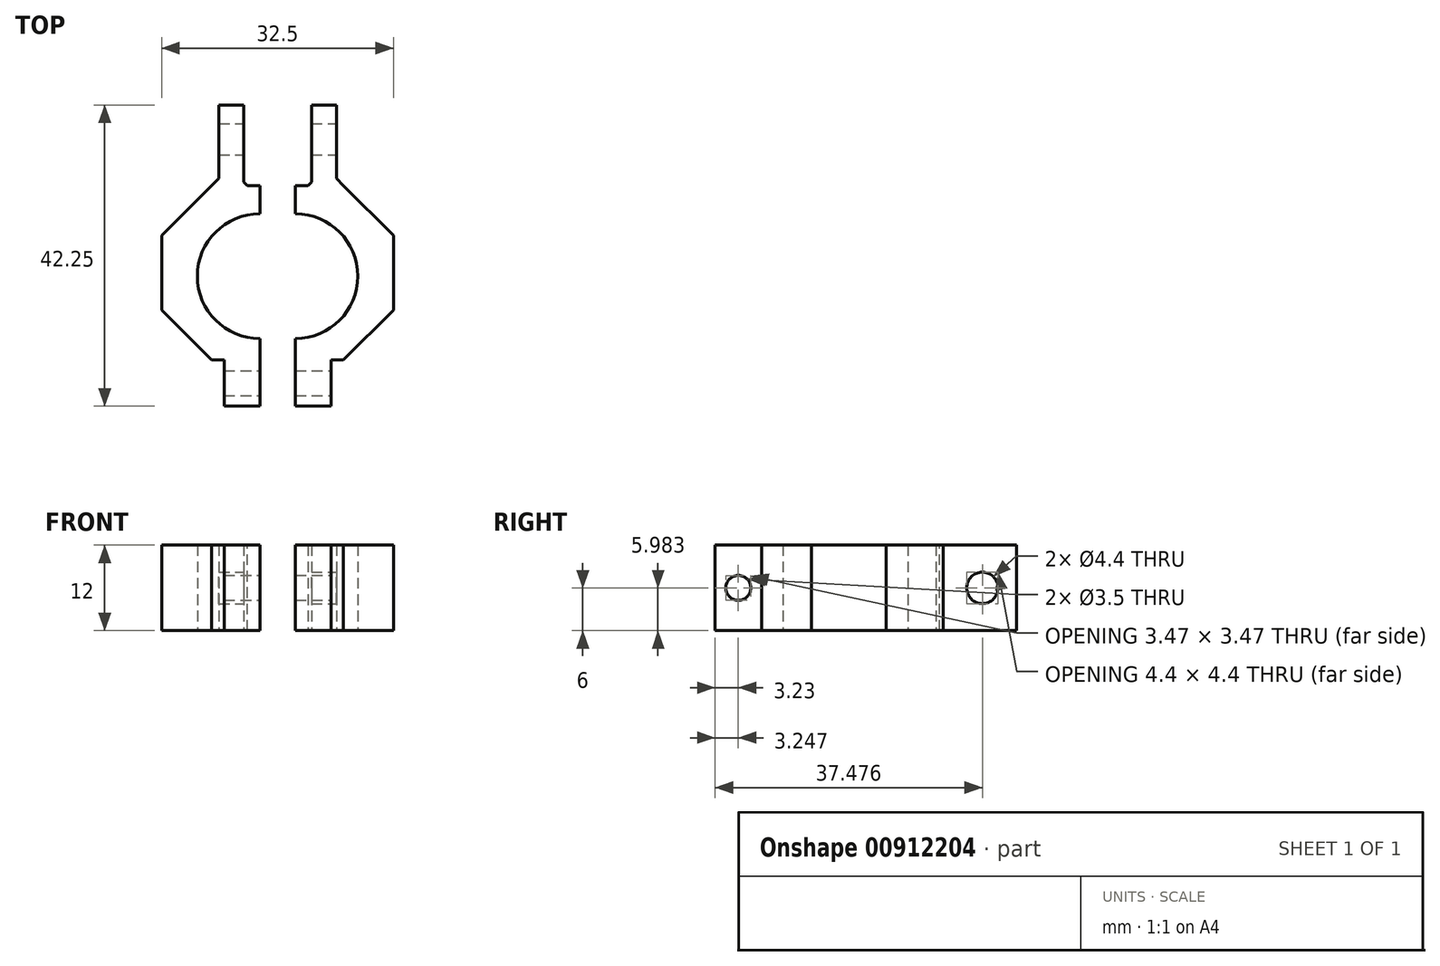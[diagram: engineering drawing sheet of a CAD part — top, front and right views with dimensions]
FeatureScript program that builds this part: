
annotation { "Feature Type Name" : "Feature", "Feature Type Description" : "" }
export const myFeature = defineFeature(function(context is Context, id is Id, definition is map)
    precondition{}
    {
        {
            var Q0;
            Q0=qCreatedBy(makeId("Top.planeOp"),FACE);
            var sketch = newSketch(context, id + "F0", { "sketchPlane" : qUnion([Q0])});
            skCircle(sketch, "E0", {"center": v(-3.1, 1.35) * mm, "radius": 8.75 * mm});
            skLineSegment(sketch, "E1", {"start": v(-11.85, 1.35) * mm, "end": v(-3.1, 1.35) * mm, "construction": true});
            skLineSegment(sketch, "E2", {"start": v(-3.1, 1.35) * mm, "end": v(5.65, 1.35) * mm, "construction": true});
            skLineSegment(sketch, "E3", {"start": v(-5.35, 1.35) * mm, "end": v(-5.35, 14.08) * mm, "construction": true});
            skLineSegment(sketch, "E4", {"start": v(-0.85, 14.08) * mm, "end": v(-0.85, 1.35) * mm, "construction": true});
            skLineSegment(sketch, "E5.bottom", {"start": v(-16.85, 25.35) * mm, "end": v(10.65, 25.35) * mm});
            skLineSegment(sketch, "E5.top", {"start": v(-16.85, -10.4) * mm, "end": v(10.65, -10.4) * mm});
            skLineSegment(sketch, "E5.left", {"start": v(-16.85, 25.35) * mm, "end": v(-16.85, -10.4) * mm});
            skLineSegment(sketch, "E5.right", {"start": v(10.65, 25.35) * mm, "end": v(10.65, -10.4) * mm});
            skLineSegment(sketch, "E6", {"start": v(-11.85, 1.35) * mm, "end": v(-16.85, 1.35) * mm, "construction": true});
            skLineSegment(sketch, "E7", {"start": v(5.65, 1.35) * mm, "end": v(10.65, 1.35) * mm, "construction": true});
            skLineSegment(sketch, "E8", {"start": v(-5.35, 14.08) * mm, "end": v(-5.35, 25.35) * mm});
            skLineSegment(sketch, "E9", {"start": v(-5.35, 14.08) * mm, "end": v(-0.85, 14.08) * mm});
            skLineSegment(sketch, "E10", {"start": v(-0.85, 14.08) * mm, "end": v(-0.85, 25.35) * mm});
            skLineSegment(sketch, "E11", {"start": v(-3.1, 1.35) * mm, "end": v(-3.1, -7.4) * mm});
            skLineSegment(sketch, "E12", {"start": v(-3.1, -7.4) * mm, "end": v(-3.1, -10.4) * mm});
            skLineSegment(sketch, "E13", {"start": v(-8.1, -10.4) * mm, "end": v(-8.1, -16.9) * mm});
            skLineSegment(sketch, "E14", {"start": v(-8.1, -16.9) * mm, "end": v(-3.1, -16.9) * mm});
            skLineSegment(sketch, "E15", {"start": v(-3.1, -16.9) * mm, "end": v(-3.1, -10.4) * mm});
            skLineSegment(sketch, "E16", {"start": v(-3.1, -16.9) * mm, "end": v(1.9, -16.9) * mm});
            skLineSegment(sketch, "E17", {"start": v(1.9, -16.9) * mm, "end": v(1.9, -10.4) * mm});
            skLineSegment(sketch, "E18", {"start": v(-3.1, 14.08) * mm, "end": v(-3.1, 10.1) * mm});
            skLineSegment(sketch, "E19", {"start": v(-8.85, 25.35) * mm, "end": v(-8.85, 14.08) * mm});
            skLineSegment(sketch, "E20", {"start": v(-8.85, 14.08) * mm, "end": v(-16.85, 14.08) * mm});
            skLineSegment(sketch, "E21", {"start": v(2.65, 25.35) * mm, "end": v(2.65, 14.08) * mm});
            skLineSegment(sketch, "E22", {"start": v(2.65, 14.08) * mm, "end": v(10.65, 14.08) * mm});
            skSolve(sketch);
        }
        {
            var Q0;
            {var subQ2=sQuery(id+"F0.wireOp",EDGE,"E13");Q0=makeQuery(id+"F0.imprint","IMPRINT",FACE,{"disambiguationData":[TD([[makeQuery(id+"F0.imprint","IMPRINT",EDGE,{"derivedFrom":subQ2}),1.0]])]});}
            var Q1;
            {var subQ1=sQuery(id+"F0.wireOp",EDGE,"E8");Q1=makeQuery(id+"F0.imprint","IMPRINT",FACE,{"disambiguationData":[TD([[makeQuery(id+"F0.imprint","IMPRINT",EDGE,{"derivedFrom":subQ1}),1.0]])]});}
            extrude(context, id + "F1", {"entities" : qUnion([Q0, Q1]), "depth" : 12 * mm, "offsetDistance" : 25 * mm});
        }
        {
            var Q0;
            {var subQ0=sQuery(id+"F0.wireOp",EDGE,"E15");Q0=makeQuery(id+"F0.imprint","IMPRINT",FACE,{"disambiguationData":[TD([[makeQuery(id+"F0.imprint","IMPRINT",EDGE,{"derivedFrom":subQ0}),-1.0]])]});}
            var Q1;
            {var subQ1=sQuery(id+"F0.wireOp",EDGE,"E10");Q1=makeQuery(id+"F0.imprint","IMPRINT",FACE,{"disambiguationData":[TD([[makeQuery(id+"F0.imprint","IMPRINT",EDGE,{"derivedFrom":subQ1}),-1.0]])]});}
            extrude(context, id + "F2", {"entities" : qUnion([Q0, Q1]), "depth" : 12 * mm, "offsetDistance" : 25 * mm});
        }
        {
            var Q0;
            Q0=makeQuery(id+"F1.opExtrude","SWEPT_EDGE",EDGE,{"disambiguationData":[OSD([sQuery(id+"F0.wireOp",EDGE,"E5.left"),sQuery(id+"F0.wireOp",EDGE,"E20")])]});
            var Q1;
            Q1=makeQuery(id+"F2.opExtrude","SWEPT_EDGE",EDGE,{"disambiguationData":[OSD([sQuery(id+"F0.wireOp",EDGE,"E5.right"),sQuery(id+"F0.wireOp",EDGE,"E22")])]});
            var Q2;
            Q2=makeQuery(id+"F1.opExtrude","SWEPT_EDGE",EDGE,{"disambiguationData":[OSD([sQuery(id+"F0.wireOp",EDGE,"E5.top"),sQuery(id+"F0.wireOp",EDGE,"E5.left")])]});
            var Q3;
            Q3=makeQuery(id+"F2.opExtrude","SWEPT_EDGE",EDGE,{"disambiguationData":[OSD([sQuery(id+"F0.wireOp",EDGE,"E5.top"),sQuery(id+"F0.wireOp",EDGE,"E5.right")])]});
            chamfer(context, id + "F3", {"entities" : qUnion([Q0, Q1, Q2, Q3]), "width" : 7 * mm, "tangentPropagation" : true});
        }
        {
            var Q0;
            Q0=makeQuery(id+"F2.opExtrude","SWEPT_FACE",FACE,{"disambiguationData":[OSD([sQuery(id+"F0.wireOp",EDGE,"E17")])]});
            var sketch = newSketch(context, id + "F4", { "sketchPlane" : qUnion([Q0])});
            skLineSegment(sketch, "E23", {"start": v(-10.4, 6) * mm, "end": v(-16.9, 6) * mm, "construction": true});
            skCircle(sketch, "E24", {"center": v(-13.65, 6) * mm, "radius": 1.75 * mm});
            skSolve(sketch);
        }
        {
            var Q0;
            Q0=makeQuery(id+"F2.opExtrude","SWEPT_FACE",FACE,{"disambiguationData":[OSD([sQuery(id+"F0.wireOp",EDGE,"E21")])]});
            var sketch = newSketch(context, id + "F5", { "sketchPlane" : qUnion([Q0])});
            skCircle(sketch, "E25", {"center": v(20.58, 6) * mm, "radius": 2.2 * mm});
            skLineSegment(sketch, "E26", {"start": v(20.58, 6) * mm, "end": v(14.08, 6) * mm, "construction": true});
            skSolve(sketch);
        }
        {
            var Q0;
            Q0 = qSketchRegion(id + "F5", true);
            extrude(context, id + "F6", {"entities" : qUnion([Q0]), "operationType" : NewBodyOperationType.REMOVE, "oppositeDirection" : true, "depth" : 25 * mm, "offsetDistance" : 25 * mm});
        }
        {
            var Q0;
            Q0=makeQuery(id+"F1.opExtrude","SWEPT_EDGE",EDGE,{"disambiguationData":[OSD([sQuery(id+"F0.wireOp",EDGE,"E19"),sQuery(id+"F0.wireOp",EDGE,"E20")])]});
            var Q1;
            Q1=makeQuery(id+"F2.opExtrude","SWEPT_EDGE",EDGE,{"disambiguationData":[OSD([sQuery(id+"F0.wireOp",EDGE,"E21"),sQuery(id+"F0.wireOp",EDGE,"E22")])]});
            chamfer(context, id + "F7", {"entities" : qUnion([Q0, Q1]), "width" : 1 * mm, "tangentPropagation" : true});
        }
        {
            var Q0;
            Q0=makeQuery(id+"F1.opExtrude","SWEPT_EDGE",EDGE,{"disambiguationData":[OSD([sQuery(id+"F0.wireOp",EDGE,"E8"),sQuery(id+"F0.wireOp",EDGE,"E9")])]});
            var Q1;
            Q1=makeQuery(id+"F2.opExtrude","SWEPT_EDGE",EDGE,{"disambiguationData":[OSD([sQuery(id+"F0.wireOp",EDGE,"E9"),sQuery(id+"F0.wireOp",EDGE,"E10")])]});
            chamfer(context, id + "F8", {"entities" : qUnion([Q0, Q1]), "width" : .5 * mm, "tangentPropagation" : true});
        }
        {
            var Q0;
            Q0=makeQuery(id+"F4.imprint","IMPRINT",FACE,{"disambiguationData":[TD([[makeQuery(id+"F4.imprint","IMPRINT",EDGE,{"derivedFrom":sQuery(id+"F4.wireOp",EDGE,"E24")}),1.0]])]});
            extrude(context, id + "F9", {"entities" : qUnion([Q0]), "operationType" : NewBodyOperationType.REMOVE, "oppositeDirection" : true, "depth" : 25 * mm, "offsetDistance" : 25 * mm});
        }
        {
            var Q0;
            Q0=makeQuery(id+"F1.opExtrude","SWEPT_FACE",FACE,{"disambiguationData":[OSD([sQuery(id+"F0.wireOp",EDGE,"E13")])]});
            var sketch = newSketch(context, id + "F10", { "sketchPlane" : qUnion([Q0])});
            skLineSegment(sketch, "E27", {"start": v(10.4, 6) * mm, "end": v(16.9, 6) * mm, "construction": true});
            skCircle(sketch, "E28", {"center": v(13.65, 6) * mm, "radius": 1.15 * mm});
            skSolve(sketch);
        }
        {
            var Q0;
            Q0=makeQuery(id+"F10.imprint","IMPRINT",FACE,{"disambiguationData":[TD([[makeQuery(id+"F10.imprint","IMPRINT",EDGE,{"derivedFrom":sQuery(id+"F10.wireOp",EDGE,"E28")}),1.0]])]});
            extrude(context, id + "F11", {"entities" : qUnion([Q0]), "operationType" : NewBodyOperationType.REMOVE, "oppositeDirection" : true, "depth" : 25 * mm, "offsetDistance" : 25 * mm});
        }
        {
            var Q0;
            Q0=makeQuery(id+"F2.opExtrude","SWEPT_BODY",BODY,{"disambiguationData":[OSD([sQuery(id+"F0.wireOp",EDGE,"E0"),sQuery(id+"F0.wireOp",EDGE,"E5.bottom"),sQuery(id+"F0.wireOp",EDGE,"E5.top"),sQuery(id+"F0.wireOp",EDGE,"E5.right"),sQuery(id+"F0.wireOp",EDGE,"E9"),sQuery(id+"F0.wireOp",EDGE,"E10"),sQuery(id+"F0.wireOp",EDGE,"E12"),sQuery(id+"F0.wireOp",EDGE,"E15"),sQuery(id+"F0.wireOp",EDGE,"E16"),sQuery(id+"F0.wireOp",EDGE,"E17"),sQuery(id+"F0.wireOp",EDGE,"E18"),sQuery(id+"F0.wireOp",EDGE,"E21"),sQuery(id+"F0.wireOp",EDGE,"E22")])]});
            transform(context, id + "F12", {"entities" : qUnion([Q0]), "transformType" : TransformType.TRANSLATION_3D, "dx" : 5 * mm, "dy" : 0 * mm, "dz" : 0 * mm, "makeCopy" : false});
        }
    });
